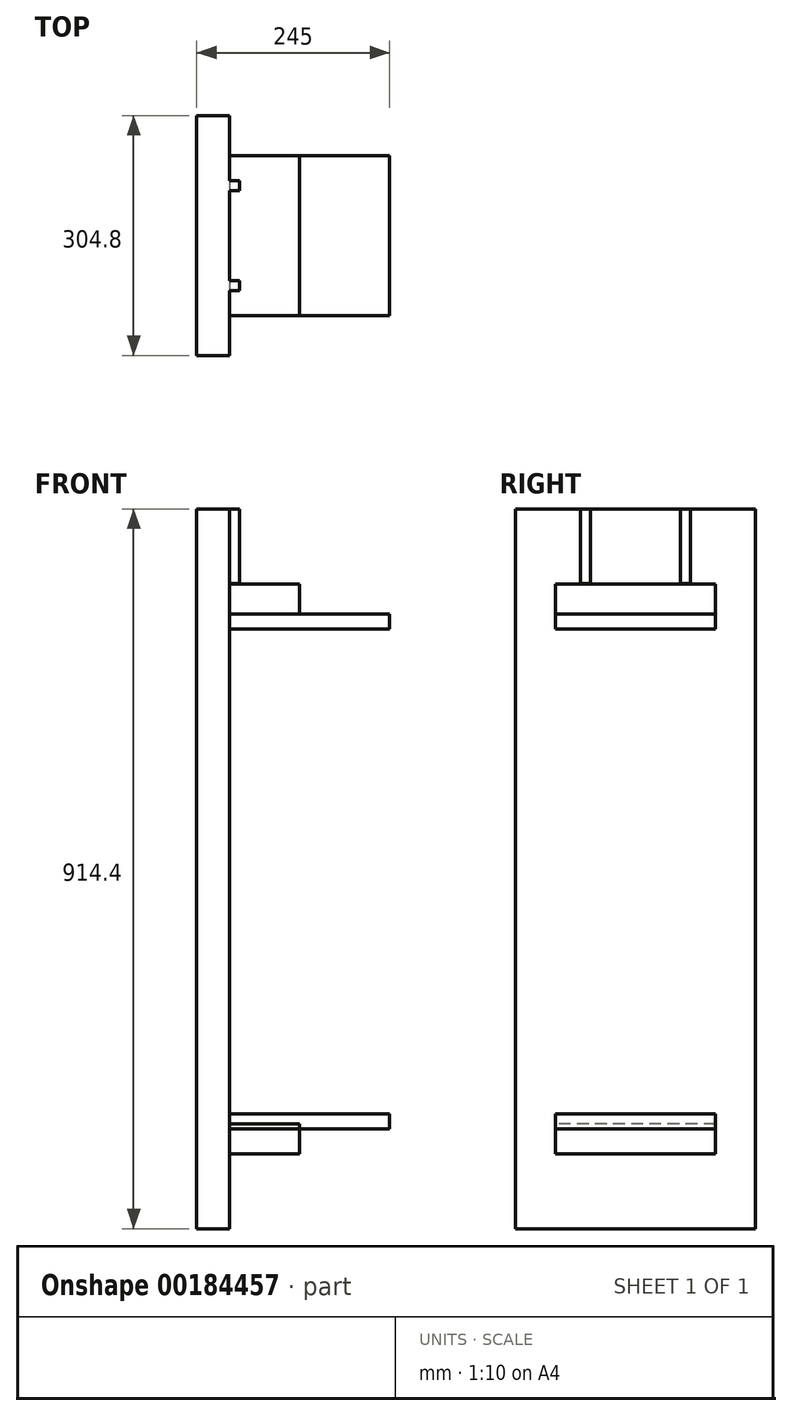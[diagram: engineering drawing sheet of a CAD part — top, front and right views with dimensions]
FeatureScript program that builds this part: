
annotation { "Feature Type Name" : "Feature", "Feature Type Description" : "" }
export const myFeature = defineFeature(function(context is Context, id is Id, definition is map)
    precondition{}
    {
        {
            var Q0;
            Q0=qCreatedBy(makeId("Top.planeOp"),FACE);
            var sketch = newSketch(context, id + "F0", { "sketchPlane" : qUnion([Q0])});
            skLineSegment(sketch, "E0.bottom", {"start": v(-8.48, -4.62) * mm, "end": v(194.72, -4.62) * mm});
            skLineSegment(sketch, "E0.top", {"start": v(-8.48, 198.58) * mm, "end": v(194.72, 198.58) * mm});
            skLineSegment(sketch, "E0.left", {"start": v(-8.48, -4.62) * mm, "end": v(-8.48, 198.58) * mm});
            skLineSegment(sketch, "E0.right", {"start": v(194.72, -4.62) * mm, "end": v(194.72, 198.58) * mm});
            skSolve(sketch);
        }
        {
            var Q0;
            Q0=makeQuery(id+"F0.imprint","IMPRINT",FACE,{"disambiguationData":[TD([[makeQuery(id+"F0.imprint","IMPRINT",EDGE,{"derivedFrom":sQuery(id+"F0.wireOp",EDGE,"E0.bottom")}),1.0]])]});
            extrude(context, id + "F1", {"entities" : qUnion([Q0]), "depth" : 19.05 * mm});
        }
        {
            var Q0;
            Q0=makeQuery(id+"F1.opExtrude","SWEPT_BODY",BODY,{"disambiguationData":[OSD([sQuery(id+"F0.wireOp",EDGE,"E0.bottom"),sQuery(id+"F0.wireOp",EDGE,"E0.top"),sQuery(id+"F0.wireOp",EDGE,"E0.left"),sQuery(id+"F0.wireOp",EDGE,"E0.right")])]});
            transform(context, id + "F2", {"entities" : qUnion([Q0]), "transformType" : TransformType.TRANSLATION_3D, "dx" : 0 * mm, "dy" : 0 * mm, "dz" : -635 * mm, "makeCopy" : true});
        }
        {
            var Q0;
            Q0=makeQuery(id+"F1.opExtrude","SWEPT_FACE",FACE,{"disambiguationData":[OSD([sQuery(id+"F0.wireOp",EDGE,"E0.left")])]});
            var sketch = newSketch(context, id + "F3", { "sketchPlane" : qUnion([Q0])});
            skLineSegment(sketch, "E1.bottom", {"start": v(-198.58, 19.05) * mm, "end": v(4.62, 19.05) * mm});
            skLineSegment(sketch, "E1.top", {"start": v(-198.58, 57.15) * mm, "end": v(4.62, 57.15) * mm});
            skLineSegment(sketch, "E1.left", {"start": v(-198.58, 19.05) * mm, "end": v(-198.58, 57.15) * mm});
            skLineSegment(sketch, "E1.right", {"start": v(4.62, 19.05) * mm, "end": v(4.62, 57.15) * mm});
            skSolve(sketch);
        }
        {
            var Q0;
            Q0=makeQuery(id+"F3.imprint","IMPRINT",FACE,{"disambiguationData":[TD([[makeQuery(id+"F3.imprint","IMPRINT",EDGE,{"derivedFrom":sQuery(id+"F3.wireOp",EDGE,"E1.bottom")}),-1.0]])]});
            extrude(context, id + "F4", {"entities" : qUnion([Q0]), "oppositeDirection" : true, "depth" : 88.9 * mm});
        }
        {
            var Q0;
            Q0=makeQuery(id+"F4.opExtrude","SWEPT_BODY",BODY,{"disambiguationData":[OSD([sQuery(id+"F3.wireOp",EDGE,"E1.bottom"),sQuery(id+"F3.wireOp",EDGE,"E1.top"),sQuery(id+"F3.wireOp",EDGE,"E1.left"),sQuery(id+"F3.wireOp",EDGE,"E1.right")])]});
            transform(context, id + "F5", {"entities" : qUnion([Q0]), "transformType" : TransformType.TRANSLATION_3D, "dx" : 0 * mm, "dy" : 0 * mm, "dz" : -685.8 * mm, "makeCopy" : true});
        }
        {
            var Q0;
            Q0=makeQuery(id+"F1.opExtrude","SWEPT_FACE",FACE,{"disambiguationData":[OSD([sQuery(id+"F0.wireOp",EDGE,"E0.top")])]});
            var sketch = newSketch(context, id + "F6", { "sketchPlane" : qUnion([Q0])});
            skLineSegment(sketch, "E2.bottom", {"start": v(8.48, 152.4) * mm, "end": v(50.28, 152.4) * mm});
            skLineSegment(sketch, "E2.top", {"start": v(8.48, -762) * mm, "end": v(50.28, -762) * mm});
            skLineSegment(sketch, "E2.left", {"start": v(8.48, 152.4) * mm, "end": v(8.48, -762) * mm});
            skLineSegment(sketch, "E2.right", {"start": v(50.28, 152.4) * mm, "end": v(50.28, -762) * mm});
            skSolve(sketch);
        }
        {
            var Q0;
            Q0 = qSketchRegion(id + "F6", true);
            extrude(context, id + "F7", {"entities" : qUnion([Q0]), "oppositeDirection" : true, "depth" : 254 * mm, "hasSecondDirection" : true, "secondDirectionOppositeDirection" : false, "secondDirectionDepth" : 50.8 * mm});
        }
        {
            var Q0;
            Q0=makeQuery(id+"F7.opExtrude","SWEPT_FACE",FACE,{"disambiguationData":[OSD([sQuery(id+"F6.wireOp",EDGE,"E2.left")])]});
            var sketch = newSketch(context, id + "F8", { "sketchPlane" : qUnion([Q0])});
            skLineSegment(sketch, "E3.bottom", {"start": v(27.13, 152.4) * mm, "end": v(39.83, 152.4) * mm});
            skLineSegment(sketch, "E3.top", {"start": v(27.13, 57.25) * mm, "end": v(39.83, 57.25) * mm});
            skLineSegment(sketch, "E3.left", {"start": v(27.13, 152.4) * mm, "end": v(27.13, 57.25) * mm});
            skLineSegment(sketch, "E3.right", {"start": v(39.83, 152.4) * mm, "end": v(39.83, 57.25) * mm});
            skLineSegment(sketch, "E4.bottom", {"start": v(154.13, 152.4) * mm, "end": v(166.83, 152.4) * mm});
            skLineSegment(sketch, "E4.top", {"start": v(154.13, 57.65) * mm, "end": v(166.83, 57.65) * mm});
            skLineSegment(sketch, "E4.left", {"start": v(154.13, 152.4) * mm, "end": v(154.13, 57.65) * mm});
            skLineSegment(sketch, "E4.right", {"start": v(166.83, 152.4) * mm, "end": v(166.83, 57.65) * mm});
            skSolve(sketch);
        }
        {
            var Q0;
            Q0=makeQuery(id+"F8.imprint","IMPRINT",FACE,{"disambiguationData":[TD([[makeQuery(id+"F8.imprint","IMPRINT",EDGE,{"derivedFrom":sQuery(id+"F8.wireOp",EDGE,"E4.bottom")}),-1.0]])]});
            var Q1;
            Q1=makeQuery(id+"F8.imprint","IMPRINT",FACE,{"disambiguationData":[TD([[makeQuery(id+"F8.imprint","IMPRINT",EDGE,{"derivedFrom":sQuery(id+"F8.wireOp",EDGE,"E3.bottom")}),-1.0]])]});
            extrude(context, id + "F9", {"entities" : qUnion([Q0, Q1]), "operationType" : NewBodyOperationType.ADD, "depth" : 12.7 * mm});
        }
    });
